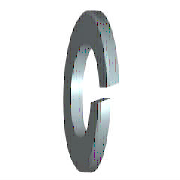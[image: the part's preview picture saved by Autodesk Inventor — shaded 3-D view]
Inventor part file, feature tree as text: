
AUTODESK INVENTOR PART (.ipt)
format: ipt  version: 2024.1 (Build 281209000, 209)  size: 126,464 bytes
history: native  units: mm (DEFAULTED — no unit token found)
features: extrude x1, other x1, plane x1
ambient origin geometry x6: Origin, YZ Plane, X Axis, Y Axis, Z Axis, Center Point
bodies: Solid1 (feature_tree), Body (feature_tree)
feature tree (3):
  extrude  "Cut"  Depth=2.6mm
  other  "Work Axis1"
  plane  "Work Plane1"
